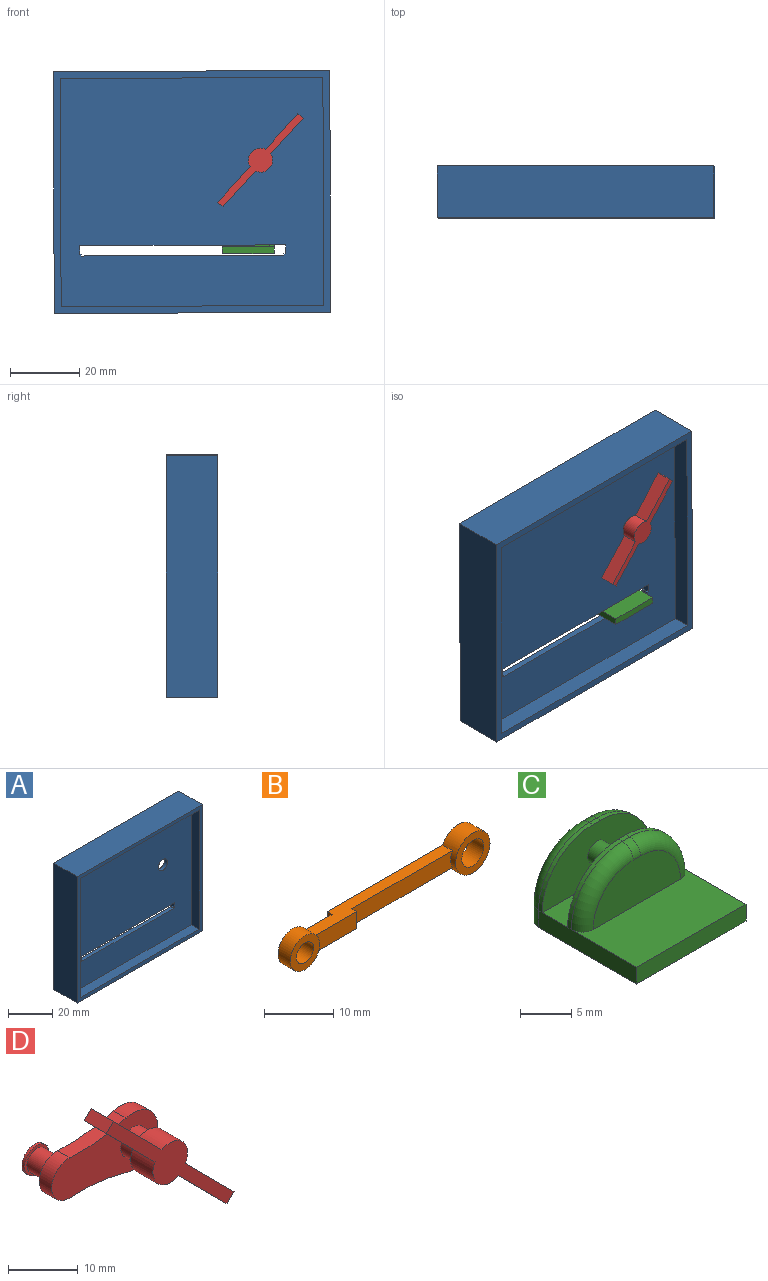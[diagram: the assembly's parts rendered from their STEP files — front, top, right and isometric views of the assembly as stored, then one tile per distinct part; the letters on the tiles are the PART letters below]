
ASSEMBLY  parts=4 mates=4
PART A: 25 faces, bbox 80x15x70 mm
  f0: plane 2.5x2mm, normal (-1,0,0), area 5mm2, adj f15,f16,f18,f22
  f1: plane 80x15mm, normal (0,0,1), area 1200mm2, adj f2,f4,f5,f14
  f2: plane 70x15mm, normal (-1,0,0), area 1050mm2, adj f1,f3,f5,f14
  f3: plane 80x15mm, normal (0,0,-1), area 1200mm2, adj f2,f4,f5,f14
  f4: plane 70x15mm, normal (1,0,0), area 1050mm2, adj f1,f3,f5,f14
  f5: plane 80x70mm, normal (0,1,0), area 584mm2, adj f1,f2,f3,f4,f6,f7,f8,f9
  f6: plane 66x8mm, normal (1,0,0), area 528mm2, adj f5,f7,f9,f16
  f7: plane 76x8mm, normal (0,0,1), area 608mm2, adj f5,f6,f8,f16
  f8: plane 66x8mm, normal (-1,0,0), area 528mm2, adj f5,f7,f9,f16
  f9: plane 76x8mm, normal (0,0,-1), area 608mm2, adj f5,f6,f8,f16
  f10: plane 76x5mm, normal (0,0,-1), area 380mm2, adj f11,f13,f14,f15
  f11: plane 66x5mm, normal (-1,0,0), area 330mm2, adj f10,f12,f14,f15
  f12: plane 76x5mm, normal (0,0,1), area 380mm2, adj f11,f13,f14,f15
  f13: plane 66x5mm, normal (1,0,0), area 330mm2, adj f10,f12,f14,f15
  f14: plane 80x70mm, normal (0,-1,0), area 584mm2, adj f1,f2,f3,f4,f10,f11,f12,f13
  f15: plane 76x66mm, normal (0,-1,0), area 4809.6mm2, adj f0,f10,f11,f12,f13,f17,f18,f19
  f16: plane 76x66mm, normal (0,1,0), area 4809.6mm2, adj f0,f6,f7,f8,f9,f17,f18,f19
  f17: cylinder r=3mm len=6mm, axis (0,1,0), area 37.7mm2, adj f15,f16
  f18: plane 59.55x2mm, normal (0,0,-1), area 119.1mm2, adj f0,f15,f16,f20
  f19: plane 58.55x2mm, normal (0,0,1), area 117.1mm2, adj f15,f16,f21,f23
  f20: plane 2.5x2mm, normal (1,0,0), area 5mm2, adj f15,f16,f18,f24
  f21: plane 2x0.5mm, normal (-1,0,0), area 1mm2, adj f15,f16,f19,f22
  f22: plane 2x0.5mm, normal (0,0,1), area 1mm2, adj f0,f15,f16,f21
  f23: plane 2x0.5mm, normal (1,0,0), area 1mm2, adj f15,f16,f19,f24
  f24: plane 2x0.5mm, normal (0,0,1), area 1mm2, adj f15,f16,f20,f23
PART B: 14 faces, bbox 41.2x3.5x7 mm
  f0: plane 3x1mm, normal (-1,0,0), area 3mm2, adj f3,f6,f7,f10
  f1: cylinder r=3.5mm len=7mm, axis (0,-1,0), area 59.8mm2, adj f3,f4,f5,f6,f7
  f2: cylinder r=2.25mm len=4.5mm, axis (0,-1,0), area 42.4mm2, adj f3,f4
  f3: plane 30.16x7mm, normal (0,1,0), area 92.4mm2, adj f0,f1,f2,f6,f7
  f4: plane 7x7mm, normal (0,-1,0), area 22.6mm2, adj f1,f2
  f5: plane 20.5x3mm, normal (0,-1,0), area 60.8mm2, adj f1,f6,f7,f8
  f6: plane 28.9x3mm, normal (0,0,1), area 60.8mm2, adj f0,f1,f3,f5,f8,f9,f10,f11
  f7: plane 28.9x3mm, normal (0,0,-1), area 60.8mm2, adj f0,f1,f3,f5,f8,f9,f10,f11
  f8: plane 3x1mm, normal (1,0,0), area 3mm2, adj f5,f6,f7,f9
  f9: plane 8.4x3mm, normal (0,-1,0), area 24.4mm2, adj f6,f7,f8,f11
  f10: plane 11x6mm, normal (0,1,0), area 34mm2, adj f0,f6,f7,f11,f12
  f11: cylinder r=3mm len=6mm, axis (0,1,0), area 40.8mm2, adj f6,f7,f9,f10,f13
  f12: cylinder r=1.75mm len=3.5mm, axis (0,1,0), area 27.5mm2, adj f10,f13
  f13: plane 6x6mm, normal (0,-1,0), area 18.7mm2, adj f11,f12
PART C: 25 faces, bbox 16.2x15x9.6 mm
  f0: plane 15x9mm, normal (0,0,1), area 113.5mm2, adj f3,f4,f5,f10,f21,f23
  f1: plane 15x3.5mm, normal (0,0,1), area 52.5mm2, adj f3,f5,f7,f9
  f2: plane 12x7.5mm, normal (0,1,0), area 77mm2, adj f6,f16,f17,f18,f19,f20
  f3: plane 13.5x2mm, normal (-1,0,0), area 27mm2, adj f0,f1,f4,f6,f12,f15,f16
  f4: plane 15x2mm, normal (0,-1,0), area 30mm2, adj f0,f3,f5,f6
  f5: plane 13.5x2mm, normal (1,0,0), area 27mm2, adj f0,f1,f4,f6,f13,f14,f20
  f6: plane 15x15mm, normal (0,0,-1), area 224mm2, adj f2,f3,f4,f5,f16,f20
  f7: plane 15x7mm, normal (0,-1,0), area 79.1mm2, adj f1,f8,f14,f15,f24
  f8: plane 1x0.5mm, normal (0,0,1), area 0.5mm2, adj f7,f14,f15,f18
  f9: plane 15x7mm, normal (0,1,0), area 79.1mm2, adj f1,f11,f12,f13,f24
  f10: plane 12x5.5mm, normal (0,-1,0), area 53mm2, adj f0,f21,f22,f23
  f11: plane 1x0.5mm, normal (0,0,1), area 0.5mm2, adj f9,f12,f13,f22
  f12: cylinder r=7mm len=7mm, axis (0,1,0), area 5.5mm2, adj f3,f9,f11,f23
  f13: cylinder r=7mm len=7mm, axis (0,-1,0), area 5.5mm2, adj f5,f9,f11,f21
  f14: cylinder r=7mm len=7mm, axis (0,-1,0), area 5.5mm2, adj f5,f7,f8,f19
  f15: cylinder r=7mm len=7mm, axis (0,1,0), area 5.5mm2, adj f3,f7,f8,f17
  f16: cylinder r=1.5mm len=2mm, axis (0,0,1), area 4.7mm2, adj f2,f3,f6,f17
  f17: torus R=5.5mm, axis (0,1,0), area 23.9mm2, adj f2,f15,f16,f18
  f18: cylinder r=1.5mm len=1.5mm, axis (1,0,0), area 2.4mm2, adj f2,f8,f17,f19
  f19: torus R=5.5mm, axis (0,1,0), area 23.9mm2, adj f2,f14,f18,f20
  f20: cylinder r=1.5mm len=2mm, axis (0,0,-1), area 4.7mm2, adj f2,f5,f6,f19
  f21: torus R=5.5mm, axis (0,-1,0), area 23.9mm2, adj f0,f10,f13,f22
  f22: cylinder r=1.5mm len=1.5mm, axis (-1,0,0), area 2.4mm2, adj f10,f11,f21,f23
  f23: torus R=5.5mm, axis (0,-1,0), area 23.9mm2, adj f0,f10,f12,f22
  f24: cylinder r=1.25mm len=3.5mm, axis (0,-1,0), area 27.5mm2, adj f7,f9
PART D: 21 faces, bbox 29.4x14.5x25.9 mm
  f0: cylinder r=2.5mm len=5mm, axis (0,-1,0), area 47.1mm2, adj f10,f13
  f1: plane 9.87x9.84mm, normal (-0.71,0,-0.71), area 62.7mm2, adj f2,f8,f9,f10
  f2: cylinder r=3.5mm len=5.17mm, axis (0,1,0), area 40.4mm2, adj f1,f3,f9,f10
  f3: plane 9.87x9.84mm, normal (-0.71,0,-0.71), area 62.7mm2, adj f2,f4,f9,f10
  f4: plane 4.5x1.42mm, normal (0.71,0,-0.71), area 9mm2, adj f3,f5,f9,f10
  f5: plane 9.87x9.84mm, normal (0.71,0,0.71), area 62.7mm2, adj f4,f6,f9,f10
  f6: cylinder r=3.5mm len=5.17mm, axis (0,1,0), area 40.4mm2, adj f5,f7,f9,f10
  f7: plane 9.87x9.84mm, normal (0.71,0,0.71), area 62.7mm2, adj f6,f8,f9,f10
  f8: plane 4.5x1.42mm, normal (-0.71,0,0.71), area 9mm2, adj f1,f7,f9,f10
  f9: plane 25.91x25.83mm, normal (0,-1,0), area 93.8mm2, adj f1,f2,f3,f4,f5,f6,f7,f8
  f10: plane 25.91x25.83mm, normal (0,1,0), area 74.2mm2, adj f0,f1,f2,f3,f4,f5,f6,f7
  f11: cylinder r=2mm len=4mm, axis (0,-1,0), area 50.3mm2, adj f18,f20
  f12: cylinder r=5mm len=10mm, axis (0,-1,0), area 46.6mm2, adj f13,f14,f16,f20
  f13: plane 21.5x10mm, normal (0,-1,0), area 140.7mm2, adj f0,f12,f14,f15,f16
  f14: cylinder r=32.08mm len=11.33mm, axis (0,-1,0), area 28.7mm2, adj f12,f13,f15,f20
  f15: cylinder r=3.5mm len=7mm, axis (0,-1,0), area 28.6mm2, adj f13,f14,f16,f20
  f16: cylinder r=32.08mm len=11.33mm, axis (0,-1,0), area 28.7mm2, adj f12,f13,f15,f20
  f17: cylinder r=2.5mm len=5mm, axis (0,1,0), area 7.9mm2, adj f18,f19
  f18: plane 5x5mm, normal (0,-1,0), area 7.1mm2, adj f11,f17
  f19: plane 5x5mm, normal (0,1,0), area 19.6mm2, adj f17
  f20: plane 21.5x10mm, normal (0,1,0), area 147.8mm2, adj f11,f12,f14,f15,f16
PLACE A rot(axis=(0,-1,0),0.2deg) t=(-18.32,-20.02,8.97)mm fixed
PLACE B rot(axis=(0,-1,0),85.3deg) t=(5.89,-20.04,57.23)mm
PLACE C rot(axis=(0,-1,0),0.2deg) t=(-48.06,-20.02,8.86)mm
PLACE D rot(axis=(0,1,0),87deg) t=(-42.67,-20.02,31.69)mm
MATE cylindrical A.f17 <-> D.f0  axis (0,-1,0) through (-18.56,-22.02,33.11)mm
MATE planar A.f22 <-> C.f6  axis (0,0,1) through (-11.81,-21.02,6.09)mm
MATE cylindrical D.f11 <-> B.f1  axis (0,1,0) through (-19.25,-12.52,46.1)mm
MATE cylindrical B.f11 <-> C.f24  axis (0,1,0) through (-22.07,-14.54,11.55)mm
